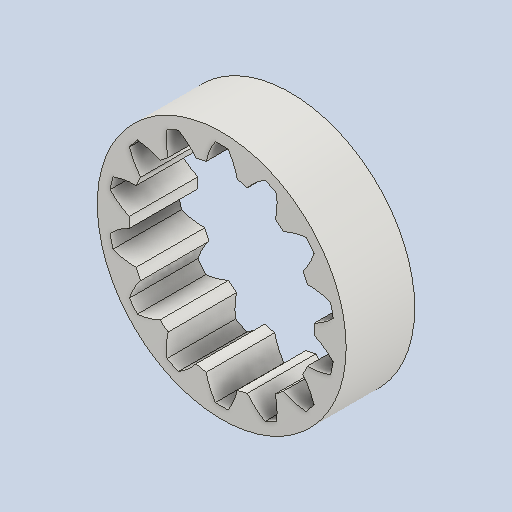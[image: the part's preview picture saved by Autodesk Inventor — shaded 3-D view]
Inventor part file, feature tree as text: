
AUTODESK INVENTOR PART (.ipt)
format: ipt  version: 2024 (Build 280153000, 153)  size: 227,840 bytes
history: native  units: mm (DEFAULTED — no unit token found)
features: plane x3, other x3, extrude x1, sketch x1
ambient origin geometry x8: Origin, YZ Plane, XZ Plane, XY Plane, X Axis, Y Axis, Z Axis, Center Point
bodies: Solid1 (feature_tree)
feature tree (8):
  extrude  "Extrusion1"  Depth=10.0mm TaperAngle=0.0deg
  plane  "Work Plane2"
  plane  "Work Plane8"
  plane  "Work Plane9"
  other  "Spur Gear"
  sketch  "Sketch1"  dims[d0=36.3mm d1=10.0mm d2=0.0mm d3=28.0mm d4=10.0mm d5=0.0mm d16=9.0mm d17=0.0mm d34=2.243995mm d39=0.0mm d45=0.0mm d47=9.0mm d50=0.0mm d51=0.0mm d52=9.0mm]
  other  "Srf1"
  other  "Pitch Diameter"
